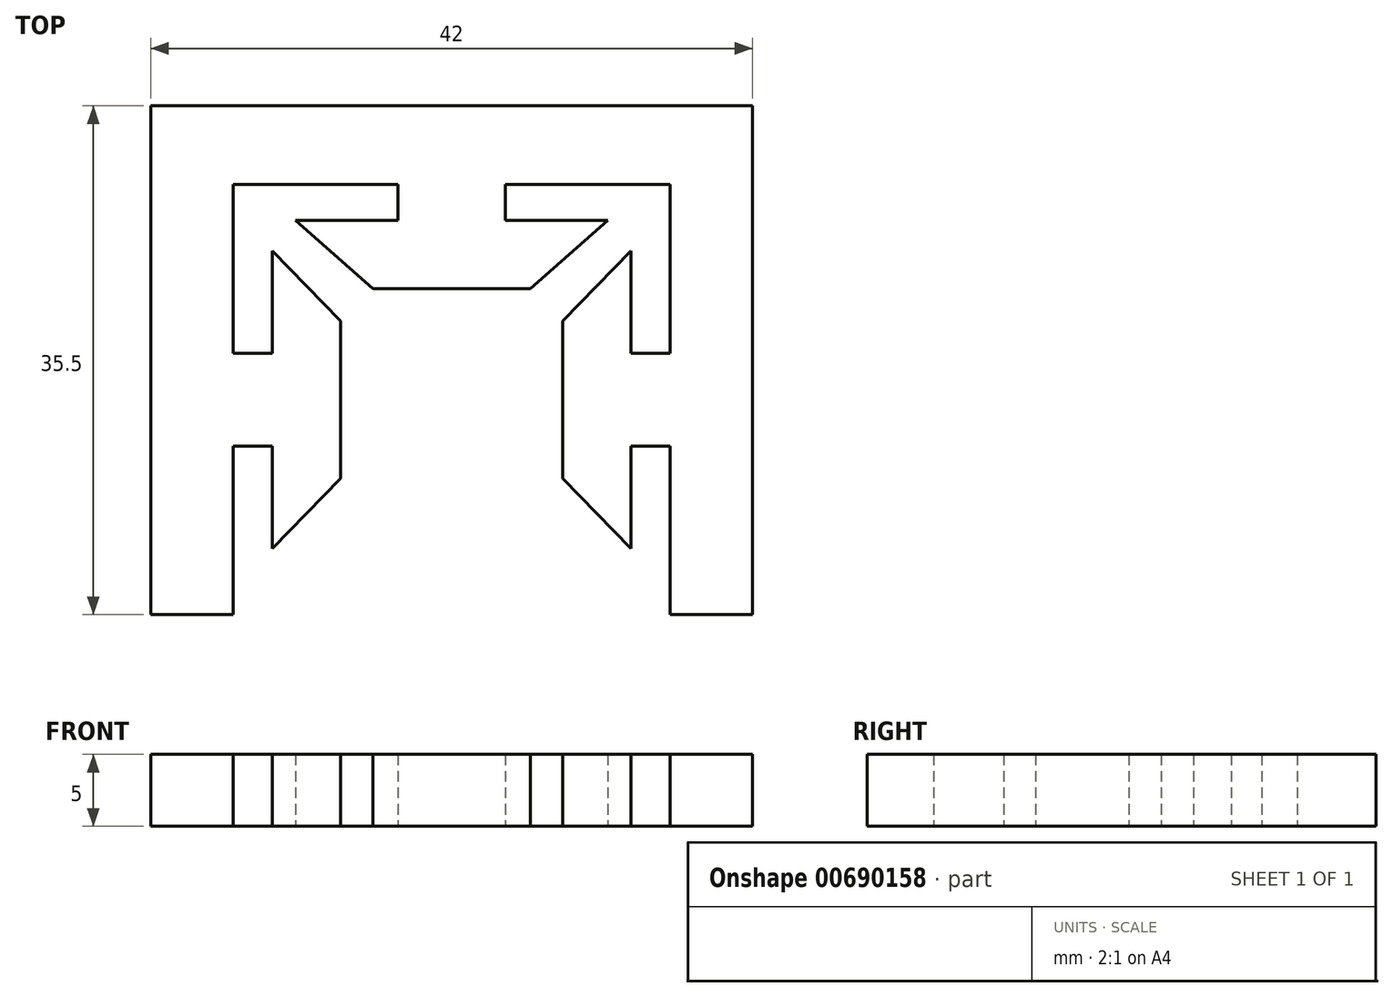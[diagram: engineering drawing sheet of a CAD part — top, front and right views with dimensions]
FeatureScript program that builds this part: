
annotation { "Feature Type Name" : "Feature", "Feature Type Description" : "" }
export const myFeature = defineFeature(function(context is Context, id is Id, definition is map)
    precondition{}
    {
        {
            var Q0;
            Q0=qCreatedBy(makeId("Top.planeOp"),FACE);
            var sketch = newSketch(context, id + "F0", { "sketchPlane" : qUnion([Q0])});
            skPoint(sketch, "E0.middle", {"position": v(0, 0) * mm});
            skLineSegment(sketch, "E1.top", {"start": v(-21, -21) * mm, "end": v(21, -21) * mm});
            skLineSegment(sketch, "E2", {"start": v(0, -21) * mm, "end": v(3.25, -21) * mm});
            skLineSegment(sketch, "E3.MirrorCS", {"start": v(0, -21) * mm, "end": v(-3.25, -21) * mm});
            skLineSegment(sketch, "E4.left", {"start": v(-21, -21) * mm, "end": v(-21, -26.5) * mm});
            skLineSegment(sketch, "E4.right", {"start": v(21, -21) * mm, "end": v(21, -26.5) * mm});
            skLineSegment(sketch, "E5", {"start": v(0, -26.5) * mm, "end": v(0, -33.75) * mm, "construction": true});
            skLineSegment(sketch, "E6", {"start": v(-3.75, -26.5) * mm, "end": v(-3.75, -29) * mm});
            skLineSegment(sketch, "E7", {"start": v(-3.75, -29) * mm, "end": v(-10.88, -29) * mm});
            skLineSegment(sketch, "E8", {"start": v(0, -33.75) * mm, "end": v(-5.5, -33.75) * mm});
            skLineSegment(sketch, "E9", {"start": v(-5.5, -33.75) * mm, "end": v(-10.88, -29) * mm});
            skLineSegment(sketch, "E10.MirrorCS", {"start": v(5.5, -33.75) * mm, "end": v(10.88, -29) * mm});
            skLineSegment(sketch, "E11.MirrorCS", {"start": v(3.75, -29) * mm, "end": v(10.88, -29) * mm});
            skLineSegment(sketch, "E12.MirrorCS", {"start": v(3.75, -26.5) * mm, "end": v(3.75, -29) * mm});
            skLineSegment(sketch, "E13.MirrorCS", {"start": v(0, -33.75) * mm, "end": v(5.5, -33.75) * mm});
            skLineSegment(sketch, "E14", {"start": v(-15, -41.5) * mm, "end": v(-7.75, -41.5) * mm, "construction": true});
            skLineSegment(sketch, "E15", {"start": v(-7.75, -41.5) * mm, "end": v(-7.75, -36) * mm});
            skLineSegment(sketch, "E16", {"start": v(-12.5, -38.25) * mm, "end": v(-12.5, -31.12) * mm});
            skLineSegment(sketch, "E17", {"start": v(-12.5, -31.12) * mm, "end": v(-7.75, -36) * mm});
            skLineSegment(sketch, "E18.MirrorCS", {"start": v(-7.75, -41.5) * mm, "end": v(-7.75, -47) * mm});
            skLineSegment(sketch, "E19.MirrorCS", {"start": v(-12.5, -51.88) * mm, "end": v(-7.75, -47) * mm});
            skLineSegment(sketch, "E20.MirrorCS", {"start": v(-12.5, -44.75) * mm, "end": v(-12.5, -51.88) * mm});
            skLineSegment(sketch, "E21", {"start": v(-15.25, -56.5) * mm, "end": v(-21, -56.5) * mm});
            skLineSegment(sketch, "E22", {"start": v(-21, -56.5) * mm, "end": v(-21, -26.5) * mm});
            skLineSegment(sketch, "E23", {"start": v(15.25, -56.5) * mm, "end": v(21, -56.5) * mm});
            skLineSegment(sketch, "E24", {"start": v(21, -56.5) * mm, "end": v(21, -26.5) * mm});
            skLineSegment(sketch, "E25", {"start": v(0, -26.5) * mm, "end": v(-15.25, -26.5) * mm});
            skLineSegment(sketch, "E26", {"start": v(-15.25, -56.5) * mm, "end": v(-15.25, -26.5) * mm});
            skLineSegment(sketch, "E27", {"start": v(-12.5, -44.75) * mm, "end": v(-15.25, -44.75) * mm});
            skLineSegment(sketch, "E28", {"start": v(-12.5, -38.25) * mm, "end": v(-15.25, -38.25) * mm});
            skLineSegment(sketch, "E29.MirrorCS", {"start": v(7.75, -41.5) * mm, "end": v(7.75, -47) * mm});
            skLineSegment(sketch, "E30.MirrorCS", {"start": v(7.75, -41.5) * mm, "end": v(7.75, -36) * mm});
            skLineSegment(sketch, "E31.MirrorCS", {"start": v(12.5, -31.12) * mm, "end": v(7.75, -36) * mm});
            skLineSegment(sketch, "E32.MirrorCS", {"start": v(12.5, -38.25) * mm, "end": v(12.5, -31.12) * mm});
            skLineSegment(sketch, "E33.MirrorCS", {"start": v(12.5, -38.25) * mm, "end": v(15.25, -38.25) * mm});
            skLineSegment(sketch, "E34.MirrorCS", {"start": v(12.5, -44.75) * mm, "end": v(15.25, -44.75) * mm});
            skLineSegment(sketch, "E35.MirrorCS", {"start": v(12.5, -44.75) * mm, "end": v(12.5, -51.88) * mm});
            skLineSegment(sketch, "E36.MirrorCS", {"start": v(12.5, -51.88) * mm, "end": v(7.75, -47) * mm});
            skLineSegment(sketch, "E37.MirrorCS", {"start": v(15.25, -56.5) * mm, "end": v(15.25, -26.5) * mm});
            skLineSegment(sketch, "E38.MirrorCS", {"start": v(0, -26.5) * mm, "end": v(15.25, -26.5) * mm});
            skSolve(sketch);
        }
        {
            var Q0;
            {var subQ2=sQuery(id+"F0.wireOp",EDGE,"E4.left");Q0=makeQuery(id+"F0.imprint","IMPRINT",FACE,{"disambiguationData":[TD([[makeQuery(id+"F0.imprint","IMPRINT",EDGE,{"derivedFrom":subQ2}),1.0]])]});}
            var Q1;
            {var subQ3=sQuery(id+"F0.wireOp",EDGE,"E6");Q1=makeQuery(id+"F0.imprint","IMPRINT",FACE,{"disambiguationData":[TD([[makeQuery(id+"F0.imprint","IMPRINT",EDGE,{"derivedFrom":subQ3}),1.0]])]});}
            var Q2;
            Q2=makeQuery(id+"F0.imprint","IMPRINT",FACE,{"disambiguationData":[TD([[makeQuery(id+"F0.imprint","IMPRINT",EDGE,{"derivedFrom":sQuery(id+"F0.wireOp",EDGE,"a72fd915-343b-4cb8-94c6-5045668657df0.MirrorCS")}),1.0]])]});
            var Q3;
            {var subQ4=sQuery(id+"F0.wireOp",EDGE,"E23");Q3=makeQuery(id+"F0.imprint","IMPRINT",FACE,{"disambiguationData":[TD([[makeQuery(id+"F0.imprint","IMPRINT",EDGE,{"derivedFrom":subQ4}),1.0]])]});}
            var Q4;
            Q4=makeQuery(id+"F0.imprint","IMPRINT",FACE,{"disambiguationData":[TD([[makeQuery(id+"F0.imprint","IMPRINT",EDGE,{"derivedFrom":sQuery(id+"F0.wireOp",EDGE,"E15")}),1.0]])]});
            var Q5;
            {var subQ3=sQuery(id+"F0.wireOp",EDGE,"xgqm9zbJ-35YR-MA57-3RnW-XfJJkj89ymEh");Q5=makeQuery(id+"F0.imprint","IMPRINT",FACE,{"disambiguationData":[TD([[makeQuery(id+"F0.imprint","IMPRINT",EDGE,{"derivedFrom":subQ3}),-1.0]])]});}
            var Q6;
            Q6=makeQuery(id+"F0.imprint","IMPRINT",FACE,{"disambiguationData":[TD([[makeQuery(id+"F0.imprint","IMPRINT",EDGE,{"derivedFrom":sQuery(id+"F0.wireOp",EDGE,"E29.MirrorCS")}),1.0]])]});
            extrude(context, id + "F1", {"entities" : qUnion([Q0, Q1, Q2, Q3, Q4, Q5, Q6]), "depth" : 5 * mm, "offsetDistance" : 25 * mm});
        }
    });
